# Revit family: Bola Sphere Flush
name_source: partatom
category: Lighting Fixtures
units: mm (PartAtom-declared; Revit-internal decimal feet)

## family parameters
Always vertical = Yes
Cut with Voids When Loaded = No
Host = Ceiling
Light Source = Yes
OmniClass Number = 23.80.70.11
OmniClass Title = Luminaries for Internal Lighting
Part Type = Normal
Room Calculation Point = No
Round Connector Dimension = Use Diameter
Shared = No

## types (6) — shared parameters
Color Filter = 16777215
Color Rendition Index = 95 CRI
Color Temperature = 2700K - 1800K (Warm Dim)
Default Elevation = 0' - 0"
Dimming Lamp Color Temperature Shift = <None>
Lifespan = 50K Hour Lifespan
Luminaire Efficacy = 65 Lumens/Watt (average)
Luminosity = 290 Lm
Power Consumption = 20W
Tilt Angle = 90.00°
Voltage = 120-277V 50/60Hz

## per-type parameters (varying)
| type | BOLA SPHERE FLUSH 4 | Photometric Web File |
| BOLA SHPERE FLUSH 4 | Yes | BOLA 6W CCT 3000K 4INCH GLOBE_IESNA2002_ V2.IES |
| BOLA SPHERE FLUSH 5 | No | BOLA 6W CCT 3000K 5INCH GLOBE_IESNA2002_ V2.IES |
| BOLA SPHERE FLUSH 6 | No | BOLA 12W CCT 3000K 6INCH GLOBE_IESNA2002_ V2.IES |
| BOLA SPHERE FLUSH 8 | No | BOLA 20W CCT 3000K 8INCH GLOBE_IESNA2002_ V2.IES |
| BOLA SPHERE FLUSH 10 | No | BOLA 20W CCT 3000K 8INCH GLOBE_IESNA2002_ V2.IES |
| BOLA SPHERE FLUSH 12 | No | BOLA 20W CCT 3000K 8INCH GLOBE_IESNA2002_ V2.IES |

type visibility flags (boolean, named after types; folded from table):
- BOLA SHPERE FLUSH 4: Yes: (none)
- BOLA SPHERE FLUSH 5: Yes: BOLA SPHERE FLUSH 5
- BOLA SPHERE FLUSH 6: Yes: BOLA SPHERE FLUSH 6
- BOLA SPHERE FLUSH 8: Yes: BOLA SPHERE FLUSH 8
- BOLA SPHERE FLUSH 10: Yes: BOLA SPHERE FLUSH 10
- BOLA SPHERE FLUSH 12: Yes: BOLA SPHERE FLUSH 12

## geometry (parser evidence)
native form markers: Sweep x3
no freeform markers — native parametric forms only
